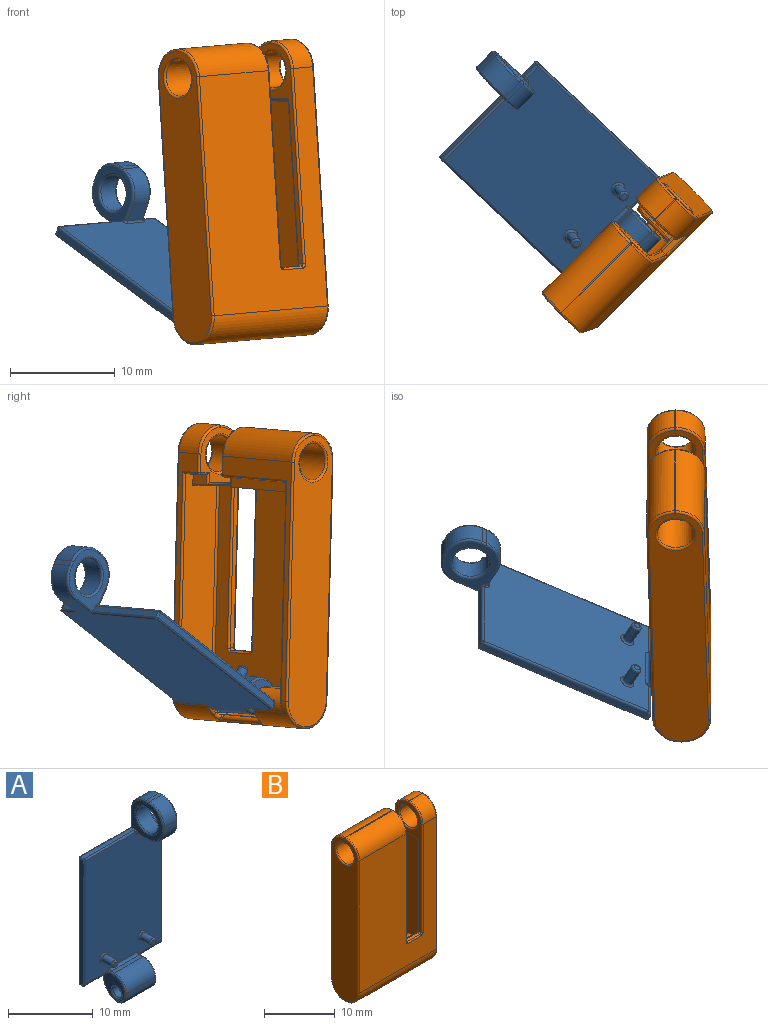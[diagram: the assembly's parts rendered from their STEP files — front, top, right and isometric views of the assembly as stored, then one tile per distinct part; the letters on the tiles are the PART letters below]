
ASSEMBLY  parts=2 mates=1
PART A: 95 faces, bbox 13.1x6x27.2 mm
  f0: plane 18.1x0.6mm, normal (1,0,0), area 10.8mm2, adj f45,f73,f74,f75,f94
  f1: plane 18.1x0.6mm, normal (-1,0,0), area 10.8mm2, adj f40,f66,f68,f69,f92
  f2: plane 1.8x0.65mm, normal (0,0,1), area 1.1mm2, adj f17,f47,f74,f77,f78
  f3: plane 17.8x12.7mm, normal (0,-1,0), area 220.2mm2, adj f16,f26,f29,f56,f59,f61,f63,f64
  f4: plane 3.8x0.3mm, normal (0,0,-1), area 1.1mm2, adj f8,f38,f66,f91
  f5: plane 3.8x0.3mm, normal (0,0,-1), area 1.1mm2, adj f9,f43,f73,f93
  f6: plane 8.5x0.65mm, normal (0,0,1), area 5.1mm2, adj f18,f42,f69,f71,f72
  f7: plane 21.5x12.7mm, normal (0,1,0), area 238.6mm2, adj f14,f22,f36,f38,f40,f41,f42,f43
  f8: plane 3.58x3.5mm, normal (-1,0,0), area 6.7mm2, adj f4,f26,f27,f28,f30,f32,f34,f36
  f9: plane 3.58x3.5mm, normal (1,0,0), area 6.7mm2, adj f5,f29,f31,f33,f35,f37,f39,f41
  f10: plane 4.7x0.6mm, normal (0,0,1), area 2.8mm2, adj f13,f16,f27,f31
  f11: plane 4.7x0.37mm, normal (0,-1,0), area 1.8mm2, adj f13,f15,f30,f35
  f12: cylinder r=0.75mm len=4.7mm, axis (1,0,0), area 22.1mm2, adj f81,f82
  f13: cylinder r=2mm len=4.7mm, axis (1,0,0), area 14.8mm2, adj f10,f11,f28,f33
  f14: cylinder r=3mm len=4.7mm, axis (1,0,0), area 16.3mm2, adj f7,f15,f34,f39
  f15: cylinder r=1.5mm len=4.7mm, axis (1,0,0), area 14mm2, adj f11,f14,f32,f37
  f16: cylinder r=0.3mm len=4.7mm, axis (-1,0,0), area 2.2mm2, adj f3,f10,f26,f29
  f17: plane 5.1x5.1mm, normal (1,0,0), area 10.4mm2, adj f2,f49,f51,f53,f55,f58,f60,f62
  f18: plane 5.1x5.1mm, normal (-1,0,0), area 10.4mm2, adj f6,f44,f46,f48,f50,f52,f54,f56
  f19: plane 2x1.8mm, normal (0,0,-1), area 3.6mm2, adj f25,f57,f61,f62
  f20: plane 2x0.5mm, normal (0,0,1), area 1mm2, adj f22,f23,f48,f53
  f21: plane 2x0.5mm, normal (0,-1,0), area 1mm2, adj f23,f25,f52,f58
  f22: cylinder r=2.5mm len=2.5mm, axis (-1,0,0), area 7.9mm2, adj f7,f20,f46,f51
  f23: cylinder r=2.5mm len=2.5mm, axis (-1,0,0), area 7.9mm2, adj f20,f21,f50,f55
  f24: cylinder r=1.75mm len=3.5mm, axis (1,0,0), area 22mm2, adj f79,f80
  f25: cylinder r=2.5mm len=2.5mm, axis (1,0,0), area 7.9mm2, adj f19,f21,f54,f60
  f26: torus R=0.5mm, axis (1,0,0), area 0.1mm2, adj f3,f8,f16,f27,f91
  f27: cylinder r=0.2mm len=0.6mm, axis (0,1,0), area 0.2mm2, adj f8,f10,f26,f28
  f28: torus R=1.8mm, axis (1,0,0), area 1mm2, adj f8,f13,f27,f30
  f29: torus R=0.5mm, axis (1,0,0), area 0.1mm2, adj f3,f9,f16,f31,f93
  f30: cylinder r=0.2mm len=0.37mm, axis (0,0,1), area 0.1mm2, adj f8,f11,f28,f32
  f31: cylinder r=0.2mm len=0.6mm, axis (0,-1,0), area 0.2mm2, adj f9,f10,f29,f33
  f32: torus R=1.3mm, axis (1,0,0), area 0.9mm2, adj f8,f15,f30,f34
  f33: torus R=1.8mm, axis (1,0,0), area 1mm2, adj f9,f13,f31,f35
  f34: torus R=2.8mm, axis (1,0,0), area 1.1mm2, adj f8,f14,f32,f36
  f35: cylinder r=0.2mm len=0.37mm, axis (0,0,-1), area 0.1mm2, adj f9,f11,f33,f37
  f36: cylinder r=0.2mm len=0.7mm, axis (0,0,-1), area 0.2mm2, adj f7,f8,f34,f38
  f37: torus R=1.3mm, axis (1,0,0), area 0.9mm2, adj f9,f15,f35,f39
  f38: cylinder r=0.2mm len=4mm, axis (1,0,0), area 1.2mm2, adj f4,f7,f36,f65
  f39: torus R=2.8mm, axis (1,0,0), area 1.1mm2, adj f9,f14,f37,f41
  f40: cylinder r=0.2mm len=18.1mm, axis (0,0,-1), area 5.7mm2, adj f1,f7,f65,f67
  f41: cylinder r=0.2mm len=0.7mm, axis (0,0,1), area 0.2mm2, adj f7,f9,f39,f43
  f42: cylinder r=0.2mm len=8.7mm, axis (-1,0,0), area 2.7mm2, adj f6,f7,f44,f67
  f43: cylinder r=0.2mm len=4.14mm, axis (1,0,0), area 1.2mm2, adj f5,f7,f41,f45,f73
  f44: cylinder r=0.2mm len=2.7mm, axis (0,0,-1), area 0.8mm2, adj f7,f18,f42,f46
  f45: cylinder r=0.2mm len=18.38mm, axis (0,0,1), area 5.7mm2, adj f0,f7,f43,f47,f73,f74
  f46: torus R=2.3mm, axis (-1,0,0), area 1.2mm2, adj f18,f22,f44,f48
  f47: cylinder r=0.2mm len=2.14mm, axis (-1,0,0), area 0.6mm2, adj f2,f7,f45,f49,f74
  f48: cylinder r=0.2mm len=0.5mm, axis (0,-1,0), area 0.2mm2, adj f18,f20,f46,f50
  f49: cylinder r=0.2mm len=2.7mm, axis (0,0,1), area 0.8mm2, adj f7,f17,f47,f51
  f50: torus R=2.3mm, axis (-1,0,0), area 1.2mm2, adj f18,f23,f48,f52
  f51: torus R=2.3mm, axis (-1,0,0), area 1.2mm2, adj f17,f22,f49,f53
  f52: cylinder r=0.2mm len=0.5mm, axis (0,0,-1), area 0.2mm2, adj f18,f21,f50,f54
  f53: cylinder r=0.2mm len=0.5mm, axis (0,1,0), area 0.2mm2, adj f17,f20,f51,f55
  f54: torus R=2.3mm, axis (-1,0,0), area 1.2mm2, adj f18,f25,f52,f57
  f55: torus R=2.3mm, axis (-1,0,0), area 1.2mm2, adj f17,f23,f53,f58
  f56: cylinder r=0.2mm len=0.2mm, axis (0,0,1), area 0mm2, adj f3,f18,f59,f72
  f57: cylinder r=0.2mm len=1.8mm, axis (0,1,0), area 0.6mm2, adj f18,f19,f54,f59
  f58: cylinder r=0.2mm len=0.5mm, axis (0,0,1), area 0.2mm2, adj f17,f21,f55,f60
  f59: torus R=0.4mm, axis (0,-1,0), area 0.1mm2, adj f3,f56,f57,f61
  f60: torus R=2.3mm, axis (-1,0,0), area 1.2mm2, adj f17,f25,f58,f62
  f61: cylinder r=0.2mm len=2mm, axis (-1,0,0), area 0.6mm2, adj f3,f19,f59,f63
  f62: cylinder r=0.2mm len=1.8mm, axis (0,-1,0), area 0.6mm2, adj f17,f19,f60,f63
  f63: torus R=0.4mm, axis (0,-1,0), area 0.1mm2, adj f3,f61,f62,f64
  f64: cylinder r=0.2mm len=0.2mm, axis (0,0,-1), area 0mm2, adj f3,f17,f63,f78
  f65: sphere r=0.2mm, area 0.1mm2, adj f38,f40,f66
  f66: cylinder r=0.2mm len=0.3mm, axis (0,-1,0), area 0.1mm2, adj f1,f4,f65,f92
  f67: sphere r=0.2mm, area 0.1mm2, adj f40,f42,f69
  f68: cylinder r=0.2mm len=17.8mm, axis (0,0,1), area 5.6mm2, adj f1,f3,f70,f92
  f69: cylinder r=0.2mm len=0.6mm, axis (0,1,0), area 0.2mm2, adj f1,f6,f67,f70
  f70: sphere r=0.2mm, area 0.1mm2, adj f68,f69,f71
  f71: cylinder r=0.2mm len=8.3mm, axis (1,0,0), area 2.6mm2, adj f3,f6,f70,f72
  f72: torus R=0.4mm, axis (0,0,-1), area 0.1mm2, adj f6,f18,f56,f71
  f73: cylinder r=0.2mm len=0.44mm, axis (0,1,0), area 0.1mm2, adj f0,f5,f43,f45,f94
  f74: cylinder r=0.2mm len=0.74mm, axis (0,-1,0), area 0.2mm2, adj f0,f2,f45,f47,f76
  f75: cylinder r=0.2mm len=17.8mm, axis (0,0,-1), area 5.6mm2, adj f0,f3,f76,f94
  f76: sphere r=0.2mm, area 0.1mm2, adj f74,f75,f77
  f77: cylinder r=0.2mm len=1.6mm, axis (1,0,0), area 0.5mm2, adj f2,f3,f76,f78
  f78: torus R=0.4mm, axis (0,0,-1), area 0.1mm2, adj f2,f17,f64,f77
  f79: torus R=1.95mm, axis (-1,0,0), area 3.6mm2, adj f18,f24
  f80: torus R=1.95mm, axis (-1,0,0), area 3.6mm2, adj f17,f24
  f81: torus R=0.95mm, axis (1,0,0), area 1.6mm2, adj f8,f12
  f82: torus R=0.95mm, axis (1,0,0), area 1.6mm2, adj f9,f12
  f83: cylinder r=0.5mm len=1.6mm, axis (0,1,0), area 5mm2, adj f89,f90
  f84: plane 0.6x0.6mm, normal (0,-1,0), area 0.3mm2, adj f90
  f85: cylinder r=0.5mm len=1.6mm, axis (0,1,0), area 5mm2, adj f87,f88
  f86: plane 0.6x0.6mm, normal (0,-1,0), area 0.3mm2, adj f88
  f87: torus R=0.7mm, axis (0,-1,0), area 1.1mm2, adj f3,f85
  f88: torus R=0.3mm, axis (0,-1,0), area 0.8mm2, adj f85,f86
  f89: torus R=0.7mm, axis (0,-1,0), area 1.1mm2, adj f3,f83
  f90: torus R=0.3mm, axis (0,-1,0), area 0.8mm2, adj f83,f84
  f91: cylinder r=0.5mm len=3.82mm, axis (-1,0,0), area 3mm2, adj f3,f4,f8,f26,f92
  f92: torus R=0.3mm, axis (1,0,0), area 0.2mm2, adj f1,f66,f68,f91
  f93: cylinder r=0.5mm len=3.82mm, axis (-1,0,0), area 3mm2, adj f3,f5,f9,f29,f94
  f94: torus R=0.3mm, axis (1,0,0), area 0.2mm2, adj f0,f73,f75,f93
PART B: 122 faces, bbox 15.7x5.9x28.7 mm
  f0: cylinder r=0.3mm len=5.02mm, axis (1,0,0), area 4.3mm2, adj f1,f23,f29,f116
  f1: bspline ~0.62x0.4mm, area 0.2mm2, adj f0,f23,f29,f40,f117
  f2: bspline ~1.07x1.05mm, area 0.5mm2, adj f29,f83,f115,f116
  f3: plane 22.9x2.6mm, normal (0,1,0), area 17.3mm2, adj f27,f29,f44,f97,f109,f110
  f4: plane 21.2x5.1mm, normal (1,0,0), area 19.2mm2, adj f58,f59,f63,f64,f67,f69,f70,f72
  f5: plane 21.2x5.1mm, normal (-1,0,0), area 19.2mm2, adj f44,f45,f48,f49,f51,f52,f54,f55
  f6: plane 3.7x2.79mm, normal (0,0,1), area 10.3mm2, adj f16,f38,f43,f120
  f7: plane 22.9x9.3mm, normal (0,1,0), area 29.4mm2, adj f29,f30,f67,f89,f105,f106
  f8: plane 2.6x0.1mm, normal (0,0,1), area 0.3mm2, adj f27,f28,f49,f98
  f9: plane 3.2x1.6mm, normal (0,0,-1), area 5.1mm2, adj f33,f47,f53,f54
  f10: plane 27.9x5.1mm, normal (-1,0,0), area 125mm2, adj f84,f85,f86,f87,f88,f89,f90,f91
  f11: plane 15.3x0.1mm, normal (0,0,-1), area 1.5mm2, adj f29,f31,f90,f93
  f12: plane 27.9x5.1mm, normal (1,0,0), area 125mm2, adj f92,f93,f94,f95,f96,f97,f98,f99
  f13: plane 9.3x0.1mm, normal (0,0,1), area 0.9mm2, adj f30,f32,f59,f85
  f14: plane 22.9x15.3mm, normal (0,-1,0), area 285.5mm2, adj f28,f31,f32,f55,f57,f62,f63,f66
  f15: plane 8.3x3.2mm, normal (0,0,-1), area 26.6mm2, adj f36,f74,f76,f77
  f16: plane 20.89x4.2mm, normal (-1,0,0), area 80.1mm2, adj f6,f33,f34,f38,f46,f47,f109
  f17: plane 3.7x2.79mm, normal (0,0,1), area 10.3mm2, adj f18,f37,f80,f113
  f18: plane 20.89x4.2mm, normal (1,0,0), area 80.1mm2, adj f17,f35,f36,f37,f77,f79,f105
  f19: plane 19.7x13.3mm, normal (0,1,0), area 198.4mm2, adj f39,f42,f43,f46,f53,f60,f65,f68
  f20: plane 2.6x0.5mm, normal (0,0,1), area 1.3mm2, adj f61,f62,f68,f69
  f21: plane 3.99x2.5mm, normal (-1,0,0), area 7.9mm2, adj f26,f40,f41,f42,f118,f119,f120
  f22: plane 3.99x2.5mm, normal (1,0,0), area 7.9mm2, adj f26,f81,f82,f83,f113,f114,f115
  f23: plane 5.3x0.59mm, normal (0,0,1), area 3.1mm2, adj f0,f1,f39,f40,f83,f116
  f24: cylinder r=1.75mm len=3.5mm, axis (1,0,0), area 28.6mm2, adj f102,f103
  f25: cylinder r=1.75mm len=9.3mm, axis (1,0,0), area 102.3mm2, adj f100,f101
  f26: cylinder r=0.5mm len=5.7mm, axis (1,0,0), area 17.9mm2, adj f21,f22
  f27: cylinder r=2.7mm len=2.7mm, axis (-1,0,0), area 11mm2, adj f3,f8,f45,f99
  f28: cylinder r=2.7mm len=2.7mm, axis (1,0,0), area 11mm2, adj f8,f14,f52,f96
  f29: cylinder r=2.7mm len=15.3mm, axis (1,0,0), area 34.4mm2, adj f0,f1,f2,f3,f7,f11,f37,f38
  f30: cylinder r=2.7mm len=9.3mm, axis (-1,0,0), area 39.4mm2, adj f7,f13,f64,f87
  f31: cylinder r=2.7mm len=15.3mm, axis (-1,0,0), area 64.9mm2, adj f11,f14,f88,f92
  f32: cylinder r=2.7mm len=9.3mm, axis (1,0,0), area 39.4mm2, adj f13,f14,f58,f84
  f33: plane 1.8x1.2mm, normal (0,1,0), area 1.8mm2, adj f9,f16,f34,f47,f51
  f34: plane 1.8x1mm, normal (0,0,-1), area 1.8mm2, adj f16,f33,f48,f110
  f35: plane 8.5x1mm, normal (0,0,-1), area 8.5mm2, adj f18,f36,f70,f106
  f36: plane 8.5x1.2mm, normal (0,1,0), area 8.5mm2, adj f15,f18,f35,f72,f77
  f37: cylinder r=1.5mm len=3.9mm, axis (1,0,0), area 11.2mm2, adj f17,f18,f29,f104,f105,f114
  f38: cylinder r=1.5mm len=3.9mm, axis (1,0,0), area 11.2mm2, adj f6,f16,f29,f108,f109,f119
  f39: cylinder r=2mm len=5.3mm, axis (-1,0,0), area 16.7mm2, adj f19,f23,f41,f82
  f40: cylinder r=0.2mm len=1.49mm, axis (0,-1,0), area 0.3mm2, adj f1,f21,f23,f41,f117
  f41: torus R=1.8mm, axis (1,0,0), area 1mm2, adj f21,f39,f40,f42
  f42: cylinder r=0.2mm len=1.2mm, axis (0,0,-1), area 0.3mm2, adj f19,f21,f41,f121
  f43: cylinder r=0.2mm len=4.2mm, axis (-1,0,0), area 1.2mm2, adj f6,f19,f46,f121
  f44: cylinder r=0.2mm len=1.8mm, axis (0,0,1), area 0.6mm2, adj f3,f5,f45,f111
  f45: torus R=2.5mm, axis (-1,0,0), area 1.3mm2, adj f5,f27,f44,f49
  f46: cylinder r=0.2mm len=18.7mm, axis (0,0,-1), area 5.8mm2, adj f16,f19,f43,f50
  f47: cylinder r=0.2mm len=3.2mm, axis (0,1,0), area 1mm2, adj f9,f16,f33,f50
  f48: cylinder r=0.2mm len=1.2mm, axis (0,-1,0), area 0.3mm2, adj f5,f34,f51,f111
  f49: cylinder r=0.2mm len=0.2mm, axis (0,-1,0), area 0mm2, adj f5,f8,f45,f52
  f50: sphere r=0.2mm, area 0.1mm2, adj f46,f47,f53
  f51: cylinder r=0.2mm len=1.2mm, axis (0,0,-1), area 0.3mm2, adj f5,f33,f48,f54
  f52: torus R=2.5mm, axis (-1,0,0), area 1.3mm2, adj f5,f28,f49,f55
  f53: cylinder r=0.2mm len=1.6mm, axis (1,0,0), area 0.5mm2, adj f9,f19,f50,f56
  f54: cylinder r=0.2mm len=3.2mm, axis (0,1,0), area 1mm2, adj f5,f9,f51,f56
  f55: cylinder r=0.2mm len=18.7mm, axis (0,0,-1), area 5.9mm2, adj f5,f14,f52,f57
  f56: torus R=0.4mm, axis (-1,0,0), area 0.1mm2, adj f5,f53,f54,f60
  f57: torus R=0.4mm, axis (0,-1,0), area 0.1mm2, adj f14,f55,f61,f62
  f58: torus R=2.5mm, axis (-1,0,0), area 1.3mm2, adj f4,f32,f59,f63
  f59: cylinder r=0.2mm len=0.2mm, axis (0,1,0), area 0mm2, adj f4,f13,f58,f64
  f60: cylinder r=0.2mm len=15.5mm, axis (0,0,1), area 4.9mm2, adj f5,f19,f56,f65
  f61: cylinder r=0.2mm len=0.5mm, axis (0,-1,0), area 0.2mm2, adj f5,f20,f57,f65
  f62: cylinder r=0.2mm len=2.6mm, axis (-1,0,0), area 0.8mm2, adj f14,f20,f57,f66
  f63: cylinder r=0.2mm len=18.7mm, axis (0,0,1), area 5.9mm2, adj f4,f14,f58,f66
  f64: torus R=2.5mm, axis (-1,0,0), area 1.3mm2, adj f4,f30,f59,f67
  f65: torus R=0.4mm, axis (0,1,0), area 0.1mm2, adj f19,f60,f61,f68
  f66: torus R=0.4mm, axis (0,-1,0), area 0.1mm2, adj f14,f62,f63,f69
  f67: cylinder r=0.2mm len=1.8mm, axis (0,0,-1), area 0.6mm2, adj f4,f7,f64,f107
  f68: cylinder r=0.2mm len=2.6mm, axis (1,0,0), area 0.8mm2, adj f19,f20,f65,f71
  f69: cylinder r=0.2mm len=0.5mm, axis (0,1,0), area 0.2mm2, adj f4,f20,f66,f71
  f70: cylinder r=0.2mm len=1.2mm, axis (0,1,0), area 0.3mm2, adj f4,f35,f72,f107
  f71: torus R=0.4mm, axis (0,1,0), area 0.1mm2, adj f19,f68,f69,f73
  f72: cylinder r=0.2mm len=1.2mm, axis (0,0,1), area 0.3mm2, adj f4,f36,f70,f74
  f73: cylinder r=0.2mm len=15.5mm, axis (0,0,-1), area 4.9mm2, adj f4,f19,f71,f75
  f74: cylinder r=0.2mm len=3.2mm, axis (0,-1,0), area 1mm2, adj f4,f15,f72,f75
  f75: torus R=0.4mm, axis (-1,0,0), area 0.1mm2, adj f4,f73,f74,f76
  f76: cylinder r=0.2mm len=8.3mm, axis (1,0,0), area 2.6mm2, adj f15,f19,f75,f78
  f77: cylinder r=0.2mm len=3.2mm, axis (0,-1,0), area 1mm2, adj f15,f18,f36,f78
  f78: sphere r=0.2mm, area 0.1mm2, adj f76,f77,f79
  f79: cylinder r=0.2mm len=18.7mm, axis (0,0,1), area 5.8mm2, adj f18,f19,f78,f80
  f80: cylinder r=0.2mm len=4.2mm, axis (-1,0,0), area 1.2mm2, adj f17,f19,f79,f112
  f81: cylinder r=0.2mm len=1.2mm, axis (0,0,1), area 0.3mm2, adj f19,f22,f82,f112
  f82: torus R=1.8mm, axis (1,0,0), area 1mm2, adj f22,f39,f81,f83
  f83: cylinder r=0.2mm len=1.49mm, axis (0,1,0), area 0.3mm2, adj f2,f22,f23,f82,f116
  f84: torus R=2.5mm, axis (-1,0,0), area 1.3mm2, adj f10,f32,f85,f86
  f85: cylinder r=0.2mm len=0.2mm, axis (0,1,0), area 0mm2, adj f10,f13,f84,f87
  f86: cylinder r=0.2mm len=22.9mm, axis (0,0,1), area 7.2mm2, adj f10,f14,f84,f88
  f87: torus R=2.5mm, axis (-1,0,0), area 1.3mm2, adj f10,f30,f85,f89
  f88: torus R=2.5mm, axis (-1,0,0), area 1.3mm2, adj f10,f31,f86,f90
  f89: cylinder r=0.2mm len=22.9mm, axis (0,0,-1), area 7.2mm2, adj f7,f10,f87,f91
  f90: cylinder r=0.2mm len=0.2mm, axis (0,-1,0), area 0mm2, adj f10,f11,f88,f91
  f91: torus R=2.5mm, axis (-1,0,0), area 1.3mm2, adj f10,f29,f89,f90
  f92: torus R=2.5mm, axis (-1,0,0), area 1.3mm2, adj f12,f31,f93,f94
  f93: cylinder r=0.2mm len=0.2mm, axis (0,1,0), area 0mm2, adj f11,f12,f92,f95
  f94: cylinder r=0.2mm len=22.9mm, axis (0,0,-1), area 7.2mm2, adj f12,f14,f92,f96
  f95: torus R=2.5mm, axis (-1,0,0), area 1.3mm2, adj f12,f29,f93,f97
  f96: torus R=2.5mm, axis (-1,0,0), area 1.3mm2, adj f12,f28,f94,f98
  f97: cylinder r=0.2mm len=22.9mm, axis (0,0,1), area 7.2mm2, adj f3,f12,f95,f99
  f98: cylinder r=0.2mm len=0.2mm, axis (0,-1,0), area 0mm2, adj f8,f12,f96,f99
  f99: torus R=2.5mm, axis (-1,0,0), area 1.3mm2, adj f12,f27,f97,f98
  f100: torus R=1.95mm, axis (-1,0,0), area 3.6mm2, adj f10,f25
  f101: torus R=1.95mm, axis (-1,0,0), area 3.6mm2, adj f4,f25
  f102: torus R=1.95mm, axis (-1,0,0), area 3.6mm2, adj f5,f24
  f103: torus R=1.95mm, axis (-1,0,0), area 3.6mm2, adj f12,f24
  f104: torus R=2.5mm, axis (1,0,0), area 0.2mm2, adj f29,f37,f105
  f105: cylinder r=0.2mm len=21.1mm, axis (0,0,1), area 6.6mm2, adj f7,f18,f37,f104,f106
  f106: cylinder r=0.2mm len=8.7mm, axis (1,0,0), area 2.7mm2, adj f7,f35,f105,f107
  f107: sphere r=0.2mm, area 0mm2, adj f67,f70,f106
  f108: torus R=2.5mm, axis (1,0,0), area 0.2mm2, adj f29,f38,f109
  f109: cylinder r=0.2mm len=21.1mm, axis (0,0,-1), area 6.6mm2, adj f3,f16,f38,f108,f110
  f110: cylinder r=0.2mm len=2mm, axis (1,0,0), area 0.6mm2, adj f3,f34,f109,f111
  f111: sphere r=0.2mm, area 0.1mm2, adj f44,f48,f110
  f112: bspline ~0.5x0.5mm, area 0.1mm2, adj f80,f81,f113
  f113: cylinder r=0.3mm len=2.79mm, axis (0,-1,0), area 1.3mm2, adj f17,f22,f112,f114
  f114: torus R=1.2mm, axis (1,0,0), area 1.3mm2, adj f22,f37,f113,f115
  f115: torus R=2.4mm, axis (1,0,0), area 0.5mm2, adj f2,f22,f29,f114
  f116: bspline ~0.62x0.4mm, area 0.2mm2, adj f0,f2,f23,f29,f83
  f117: bspline ~1.06x1.04mm, area 0.5mm2, adj f1,f29,f40,f118
  f118: torus R=2.4mm, axis (1,0,0), area 0.5mm2, adj f21,f29,f117,f119
  f119: torus R=1.2mm, axis (1,0,0), area 1.3mm2, adj f21,f38,f118,f120
  f120: cylinder r=0.3mm len=2.79mm, axis (0,1,0), area 1.3mm2, adj f6,f21,f119,f121
  f121: bspline ~0.5x0.5mm, area 0.1mm2, adj f42,f43,f120
PLACE A rot(axis=(-0.77,-0.37,0.52),73.8deg) t=(9.07,-4.33,-5)mm
PLACE B rot(axis=(0,-0.09,1),44.9deg) t=(14.09,-10.03,2.46)mm
MATE revolute B.f26 <-> A.f12  axis (0.71,0.7,0.06) through (18.43,-9.47,-7.63)mm
